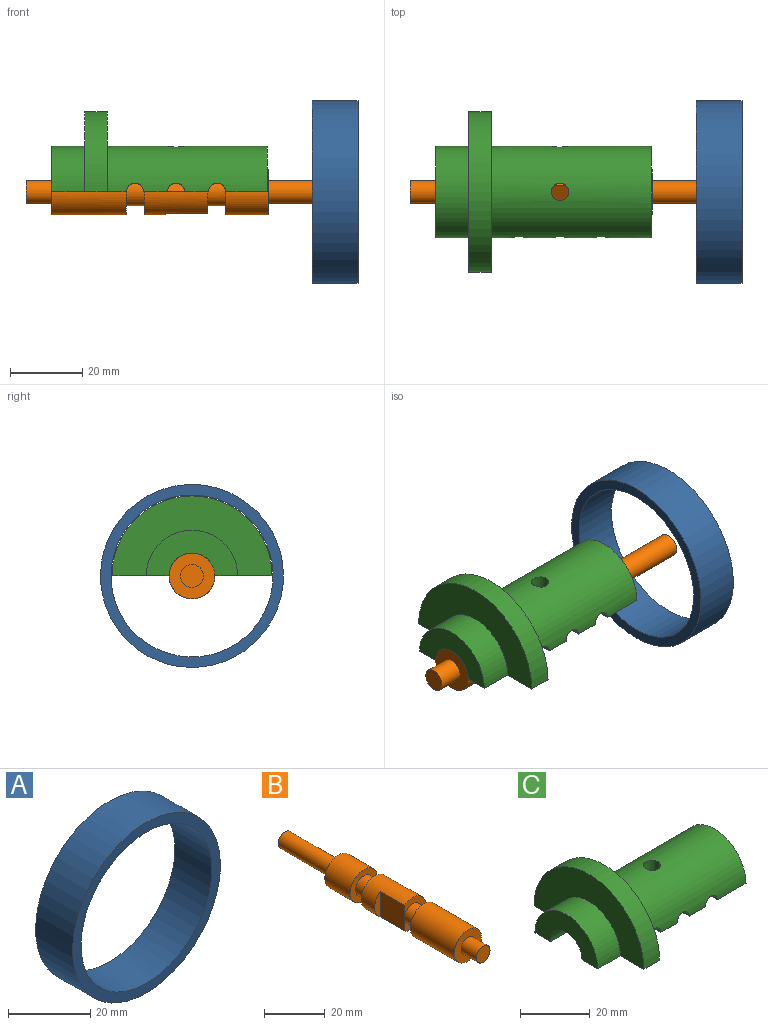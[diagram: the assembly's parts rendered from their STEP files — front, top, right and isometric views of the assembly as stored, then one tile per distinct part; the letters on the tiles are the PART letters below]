
ASSEMBLY  parts=3 mates=2
PART A: 4 faces, bbox 50.8x12.7x50.8 mm
  f0: cylinder r=22.5mm len=45mm, axis (0,1,0), area 1795.4mm2, adj f2,f3
  f1: cylinder r=25.4mm len=50.8mm, axis (0,1,0), area 2026.8mm2, adj f2,f3
  f2: plane 50.8x50.8mm, normal (0,-1,0), area 436.4mm2, adj f0,f1
  f3: plane 50.8x50.8mm, normal (0,1,0), area 436.4mm2, adj f0,f1
PART B: 21 faces, bbox 12.7x92.2x12.7 mm
  f0: cylinder r=6.35mm len=20.7mm, axis (0,-1,0), area 823.1mm2, adj f3,f8,f14,f15
  f1: cylinder r=6.35mm len=17.53mm, axis (0,-1,0), area 430.4mm2, adj f2,f7,f12,f13,f16,f17
  f2: plane 12.7x10.16mm, normal (0,1,0), area 63mm2, adj f1,f9,f13
  f3: plane 12.7x12.7mm, normal (0,-1,0), area 95mm2, adj f0,f4
  f4: cylinder r=3.17mm len=7.11mm, axis (0,1,0), area 141.9mm2, adj f3,f5
  f5: plane 6.35x6.35mm, normal (0,-1,0), area 31.7mm2, adj f4
  f6: cylinder r=3.81mm len=7.62mm, axis (0,-1,0), area 121.6mm2, adj f7,f8
  f7: plane 12.7x10.16mm, normal (0,-1,0), area 63mm2, adj f1,f6,f16
  f8: plane 12.7x10.16mm, normal (0,1,0), area 63mm2, adj f0,f6,f14
  f9: cylinder r=3.81mm len=7.62mm, axis (0,1,0), area 121.6mm2, adj f2,f10
  f10: plane 12.7x12.7mm, normal (0,-1,0), area 81.1mm2, adj f9,f11
  f11: cylinder r=6.35mm len=12.7mm, axis (0,-1,0), area 471.2mm2, adj f10,f19
  f12: plane 10.16x2.54mm, normal (0,1,0), area 18mm2, adj f1,f13
  f13: plane 11.64x10.16mm, normal (1,0,0), area 118.3mm2, adj f1,f2,f12
  f14: plane 10.16x0.24mm, normal (-1,0,0), area 2.5mm2, adj f0,f8,f15
  f15: plane 10.16x2.54mm, normal (0,1,0), area 18mm2, adj f0,f14
  f16: plane 11.19x10.16mm, normal (-1,0,0), area 113.7mm2, adj f1,f7,f17
  f17: plane 10.16x2.54mm, normal (0,-1,0), area 18mm2, adj f1,f16
  f18: cylinder r=3.17mm len=24.89mm, axis (0,-1,0), area 496.6mm2, adj f19,f20
  f19: plane 12.7x12.7mm, normal (0,1,0), area 95mm2, adj f11,f18
  f20: plane 6.35x6.35mm, normal (0,1,0), area 31.7mm2, adj f18
PART C: 19 faces, bbox 59.9x44.5x22.2 mm
  f0: cylinder r=6.35mm len=59.94mm, axis (-1,0,0), area 1139.9mm2, adj f2,f3,f8,f9,f10,f11,f12,f13
  f1: cylinder r=12.7mm len=44.45mm, axis (-1,0,0), area 1718.3mm2, adj f3,f4,f8,f9,f10,f11,f12,f13
  f2: plane 25.4x12.7mm, normal (-1,0,0), area 190mm2, adj f0,f7,f13,f16
  f3: plane 25.4x12.7mm, normal (1,0,0), area 190mm2, adj f0,f1,f14,f18
  f4: plane 44.45x22.23mm, normal (1,0,0), area 522.5mm2, adj f1,f5,f13,f16
  f5: cylinder r=22.23mm len=44.45mm, axis (-1,0,0), area 443.4mm2, adj f4,f6,f13,f16
  f6: plane 44.45x22.23mm, normal (-1,0,0), area 522.5mm2, adj f5,f7,f13,f16
  f7: cylinder r=12.7mm len=25.4mm, axis (-1,0,0), area 364.8mm2, adj f2,f6,f13,f16
  f8: cylinder r=2.41mm len=6.83mm, axis (0,-1,0), area 49.1mm2, adj f0,f1,f17,f18
  f9: cylinder r=2.41mm len=6.83mm, axis (0,-1,0), area 49.1mm2, adj f0,f1,f15,f17
  f10: cylinder r=2.41mm len=6.83mm, axis (0,-1,0), area 49.1mm2, adj f0,f1,f15,f16
  f11: cylinder r=2.41mm len=6.83mm, axis (0,1,0), area 49.1mm2, adj f0,f1,f13,f14
  f12: cylinder r=2.41mm len=6.83mm, axis (0,0,1), area 98.1mm2, adj f0,f1
  f13: plane 32.13x15.88mm, normal (0,0,-1), area 264.5mm2, adj f0,f1,f2,f4,f5,f6,f7,f11
  f14: plane 22.99x6.35mm, normal (0,0,-1), area 146mm2, adj f0,f1,f3,f11
  f15: plane 6.6x6.35mm, normal (0,0,-1), area 41.9mm2, adj f0,f1,f9,f10
  f16: plane 20.7x15.88mm, normal (0,0,-1), area 191.9mm2, adj f0,f1,f2,f4,f5,f6,f7,f10
  f17: plane 6.6x6.35mm, normal (0,0,-1), area 41.9mm2, adj f0,f1,f8,f9
  f18: plane 11.56x6.35mm, normal (0,0,-1), area 73.4mm2, adj f0,f1,f3,f8
PLACE A rot(axis=(0.29,-0.29,0.91),95.4deg) t=(68.76,26.94,-0.98)mm
PLACE B rot(axis=(0.66,0.66,-0.34),142.4deg) t=(-3.63,26.94,-0.98)mm
PLACE C t=(-3.63,26.94,-0.98)mm fixed
MATE fastened A.f1 <-> B.f4  axis (1,0,0) through (81.46,26.94,-0.98)mm
MATE revolute B.f0 <-> C.f0  axis (-1,0,0) through (-3.63,26.94,-0.98)mm
